# Revit family: deceuninck_okonniy_blok_odnostvorchatiy_s_framugoi_sverhu_i_snizu
name_source: partatom
category: Окна
revit_build: Autodesk Revit 2016 (Build: 20150714_1515(x64)
units: mm (PartAtom-declared; Revit-internal decimal feet)

## family parameters
Всегда вертикально = Да
Заголовок OmniClass = Windows
Номер OmniClass = 23.30.20.00
Общий = Нет
Основа = Стена
При загрузке вырезать с полостями = Нет
Точка расчета площади = Нет

## types (1)
- Энвин ЭКО-60
    Rед = 1.0000 (м²·K)/Вт
    Rпрофиля = 0.6800 (м²·K)/Вт
    Rстеклопакета = 0.7600 (м²·K)/Вт
    λ краевой зоны стеклопакета = 0.0600 (м²·K)/Вт
    Аналитическая конструкция = <Нет>
    Артикул импоста/армирование импоста = TE 60D  /  20 x 35
    Артикул рамы/армирование рамы = LE 60D  /  AR1
    Артикул створки/армирование рстворки = ZE 60D  /  AR1
    Высота = 0 мм
    Высота подоконника по умолчанию = 800 мм
    Высота профиля имоста = 82 мм
    Высота профиля рамы = 62 мм
    Высота профиля створки = 76 мм
    ГОСТ = ГОСТ 30673-2013
    Замыкание стены = По основе
    Класс профиля = Тип В
    Материал-Отлив = Лист оцинкованый, белый
    Материал-Подоконник = ПВХ, белый
    Материал-Рама = <По категории>
    Материал-Стеклопакет = <По категории>
    Монтажный зазор.Боковой = 20 мм
    Наименование = Окно 1-створчатое с верхними и нижними фрамугами Энвин ЭКО-60
    Огнестойкость = Е-15
    Примерная высота = 0 мм
    Примерная ширина = 0 мм
    Профильная система = Энвин ЭКО 60
    Стеклопакет.Толщина = 32 мм
    Толщина стеклопакета = 32
    Ширина = 0 мм
    Ширина профиля = 60 мм

## geometry (parser evidence)
native form markers: Blend x4
no freeform markers — native parametric forms only
